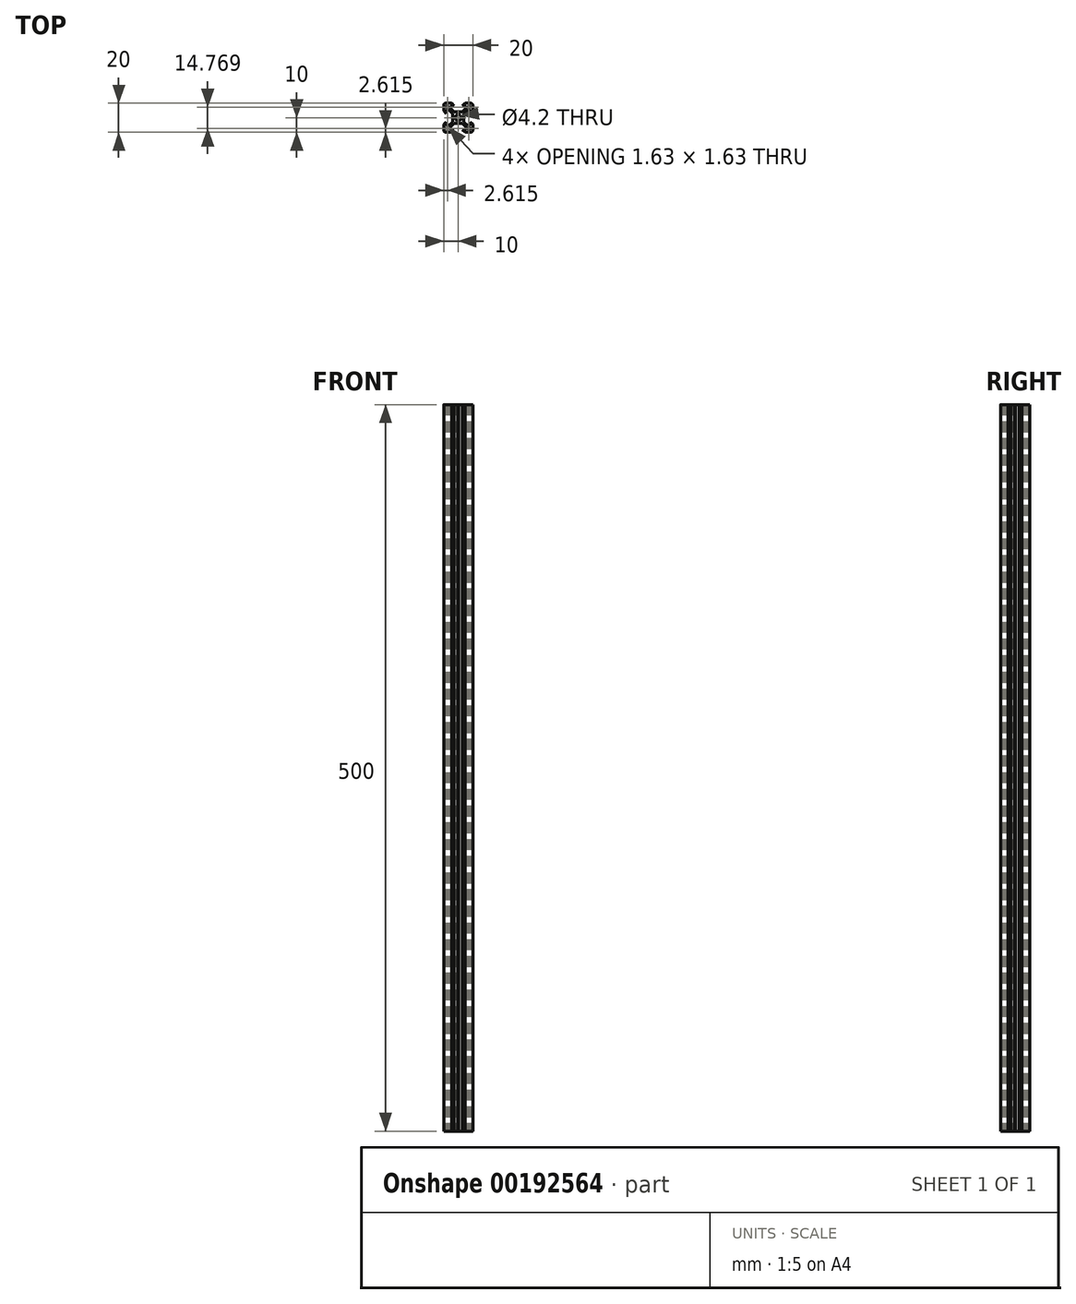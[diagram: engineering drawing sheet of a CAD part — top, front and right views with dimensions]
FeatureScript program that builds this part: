
annotation { "Feature Type Name" : "Feature", "Feature Type Description" : "" }
export const myFeature = defineFeature(function(context is Context, id is Id, definition is map)
    precondition{}
    {
        {
            var Q0;
            Q0=qCreatedBy(makeId("Top.planeOp"),FACE);
            var sketch = newSketch(context, id + "F0", { "sketchPlane" : qUnion([Q0])});
            skLineSegment(sketch, "E0", {"start": v(10, 8.5) * mm, "end": v(10, 4.64) * mm});
            skLineSegment(sketch, "E1", {"start": v(8.5, -10) * mm, "end": v(4.64, -10) * mm});
            skLineSegment(sketch, "E2", {"start": v(-10, -8.5) * mm, "end": v(-10, -4.64) * mm});
            skLineSegment(sketch, "E3", {"start": v(-8.5, 10) * mm, "end": v(-4.64, 10) * mm});
            skLineSegment(sketch, "E4.0", {"start": v(-5.5, 8.2) * mm, "end": v(-2.84, 8.2) * mm});
            skLineSegment(sketch, "E4.1", {"start": v(-8.2, -5.5) * mm, "end": v(-8.2, -2.84) * mm});
            skLineSegment(sketch, "E4.2", {"start": v(5.5, -8.2) * mm, "end": v(2.84, -8.2) * mm});
            skLineSegment(sketch, "E4.3", {"start": v(8.2, 5.5) * mm, "end": v(8.2, 2.84) * mm});
            skLineSegment(sketch, "E5.trimOffspring", {"start": v(4.64, 10) * mm, "end": v(8.5, 10) * mm});
            skPoint(sketch, "E6.start.orphan", {"position": v(0, 10) * mm});
            skLineSegment(sketch, "E7", {"start": v(-2.84, 8.2) * mm, "end": v(-4.64, 10) * mm});
            skLineSegment(sketch, "E8.trimOffspring", {"start": v(2.84, 8.2) * mm, "end": v(5.5, 8.2) * mm});
            skLineSegment(sketch, "E9.MirrorCS", {"start": v(2.84, 8.2) * mm, "end": v(4.64, 10) * mm});
            skLineSegment(sketch, "E10.MirrorCS", {"start": v(2.84, -8.2) * mm, "end": v(4.64, -10) * mm});
            skLineSegment(sketch, "E11.MirrorCS", {"start": v(-2.84, -8.2) * mm, "end": v(-4.64, -10) * mm});
            skLineSegment(sketch, "E12.trimOffspring", {"start": v(-2.84, -8.2) * mm, "end": v(-5.5, -8.2) * mm});
            skLineSegment(sketch, "E13.trimOffspring", {"start": v(-4.64, -10) * mm, "end": v(-8.5, -10) * mm});
            skLineSegment(sketch, "E14", {"start": v(-8.2, 2.84) * mm, "end": v(-10, 4.64) * mm});
            skLineSegment(sketch, "E15", {"start": v(-8.2, -2.84) * mm, "end": v(-10, -4.64) * mm});
            skLineSegment(sketch, "E16.trimOffspring", {"start": v(-10, 4.64) * mm, "end": v(-10, 8.5) * mm});
            skLineSegment(sketch, "E17.trimOffspring", {"start": v(-8.2, 2.84) * mm, "end": v(-8.2, 5.5) * mm});
            skLineSegment(sketch, "E18.MirrorCS", {"start": v(8.2, 2.84) * mm, "end": v(10, 4.64) * mm});
            skLineSegment(sketch, "E19.MirrorCS", {"start": v(8.2, -2.84) * mm, "end": v(10, -4.64) * mm});
            skLineSegment(sketch, "E20.trimOffspring", {"start": v(8.2, -2.84) * mm, "end": v(8.2, -5.5) * mm});
            skLineSegment(sketch, "E21.trimOffspring", {"start": v(10, -4.64) * mm, "end": v(10, -8.5) * mm});
            skCircle(sketch, "E22", {"center": v(0, 0) * mm, "radius": 2.1 * mm});
            skLineSegment(sketch, "E23", {"start": v(-6.56, 5.5) * mm, "end": v(-3.9, 2.84) * mm});
            skLineSegment(sketch, "E24", {"start": v(-5.5, 6.56) * mm, "end": v(-2.84, 3.9) * mm});
            skLineSegment(sketch, "E25", {"start": v(-5.5, 6.56) * mm, "end": v(-5.5, 8.2) * mm});
            skLineSegment(sketch, "E26", {"start": v(-6.56, 5.5) * mm, "end": v(-8.2, 5.5) * mm});
            skLineSegment(sketch, "E27", {"start": v(6.56, 5.5) * mm, "end": v(3.9, 2.84) * mm});
            skLineSegment(sketch, "E28", {"start": v(5.5, 6.56) * mm, "end": v(2.84, 3.9) * mm});
            skLineSegment(sketch, "E29", {"start": v(-6.56, -5.5) * mm, "end": v(-8.2, -5.5) * mm});
            skLineSegment(sketch, "E30", {"start": v(-5.5, -6.56) * mm, "end": v(-5.5, -8.2) * mm});
            skLineSegment(sketch, "E31", {"start": v(5.5, 6.56) * mm, "end": v(5.5, 8.2) * mm});
            skLineSegment(sketch, "E32", {"start": v(6.56, 5.5) * mm, "end": v(8.2, 5.5) * mm});
            skLineSegment(sketch, "E33", {"start": v(5.5, -6.56) * mm, "end": v(5.5, -8.2) * mm});
            skLineSegment(sketch, "E34", {"start": v(6.56, -5.5) * mm, "end": v(8.2, -5.5) * mm});
            skLineSegment(sketch, "E35.trimOffspring", {"start": v(2.84, -3.9) * mm, "end": v(5.5, -6.56) * mm});
            skLineSegment(sketch, "E36.trimOffspring", {"start": v(-2.84, -3.9) * mm, "end": v(-5.5, -6.56) * mm});
            skLineSegment(sketch, "E37.trimOffspring", {"start": v(-3.9, -2.84) * mm, "end": v(-6.56, -5.5) * mm});
            skLineSegment(sketch, "E38.trimOffspring", {"start": v(3.9, -2.84) * mm, "end": v(6.56, -5.5) * mm});
            skLineSegment(sketch, "E39", {"start": v(-3.9, -2.84) * mm, "end": v(-3.9, -0.25) * mm});
            skLineSegment(sketch, "E40", {"start": v(-2.84, 3.9) * mm, "end": v(-0.25, 3.9) * mm});
            skLineSegment(sketch, "E41", {"start": v(-2.84, -3.9) * mm, "end": v(-0.25, -3.9) * mm});
            skLineSegment(sketch, "E42", {"start": v(3.9, 2.84) * mm, "end": v(3.9, 0.25) * mm});
            skLineSegment(sketch, "E43", {"start": v(-8.2, 6.57) * mm, "end": v(-8.2, 8.2) * mm});
            skLineSegment(sketch, "E44", {"start": v(-6.57, 8.2) * mm, "end": v(-8.2, 8.2) * mm});
            skLineSegment(sketch, "E45", {"start": v(-8.2, 6.57) * mm, "end": v(-7.63, 6.57) * mm});
            skLineSegment(sketch, "E46", {"start": v(-6.57, 8.2) * mm, "end": v(-6.57, 7.63) * mm});
            skLineSegment(sketch, "E47", {"start": v(-7.63, 6.57) * mm, "end": v(-6.57, 7.63) * mm});
            skLineSegment(sketch, "E48.MirrorCS", {"start": v(6.57, 8.2) * mm, "end": v(8.2, 8.2) * mm});
            skLineSegment(sketch, "E49.MirrorCS", {"start": v(8.2, 6.57) * mm, "end": v(8.2, 8.2) * mm});
            skLineSegment(sketch, "E50.MirrorCS", {"start": v(8.2, 6.57) * mm, "end": v(7.63, 6.57) * mm});
            skLineSegment(sketch, "E51.MirrorCS", {"start": v(7.63, 6.57) * mm, "end": v(6.57, 7.63) * mm});
            skLineSegment(sketch, "E52.MirrorCS", {"start": v(6.57, 8.2) * mm, "end": v(6.57, 7.63) * mm});
            skLineSegment(sketch, "E53.MirrorCS", {"start": v(6.57, -8.2) * mm, "end": v(6.57, -7.63) * mm});
            skLineSegment(sketch, "E54.MirrorCS", {"start": v(8.2, -6.57) * mm, "end": v(7.63, -6.57) * mm});
            skLineSegment(sketch, "E55.MirrorCS", {"start": v(7.63, -6.57) * mm, "end": v(6.57, -7.63) * mm});
            skLineSegment(sketch, "E56.MirrorCS", {"start": v(6.57, -8.2) * mm, "end": v(8.2, -8.2) * mm});
            skLineSegment(sketch, "E57.MirrorCS", {"start": v(8.2, -6.57) * mm, "end": v(8.2, -8.2) * mm});
            skLineSegment(sketch, "E58.MirrorCS", {"start": v(-6.57, -8.2) * mm, "end": v(-8.2, -8.2) * mm});
            skLineSegment(sketch, "E59.MirrorCS", {"start": v(-8.2, -6.57) * mm, "end": v(-7.63, -6.57) * mm});
            skLineSegment(sketch, "E60.MirrorCS", {"start": v(-8.2, -6.57) * mm, "end": v(-8.2, -8.2) * mm});
            skLineSegment(sketch, "E61.MirrorCS", {"start": v(-7.63, -6.57) * mm, "end": v(-6.57, -7.63) * mm});
            skLineSegment(sketch, "E62.MirrorCS", {"start": v(-6.57, -8.2) * mm, "end": v(-6.57, -7.63) * mm});
            skPoint(sketch, "E63.visualSharp", {"position": v(-10, 10) * mm});
            skArc(sketch, "E63.filletArc", {"start": v(-8.5, 10) * mm, "mid": v(-9.56, 9.56) * mm, "end": v(-10, 8.5) * mm});
            skPoint(sketch, "E64.visualSharp", {"position": v(10, 10) * mm});
            skArc(sketch, "E64.filletArc", {"start": v(10, 8.5) * mm, "mid": v(9.56, 9.56) * mm, "end": v(8.5, 10) * mm});
            skPoint(sketch, "E65.visualSharp", {"position": v(10, -10) * mm});
            skArc(sketch, "E65.filletArc", {"start": v(8.5, -10) * mm, "mid": v(9.56, -9.56) * mm, "end": v(10, -8.5) * mm});
            skPoint(sketch, "E66.visualSharp", {"position": v(-10, -10) * mm});
            skArc(sketch, "E66.filletArc", {"start": v(-10, -8.5) * mm, "mid": v(-9.56, -9.56) * mm, "end": v(-8.5, -10) * mm});
            skLineSegment(sketch, "E67", {"start": v(-3.65, 0) * mm, "end": v(-3.9, 0.25) * mm});
            skLineSegment(sketch, "E68.MirrorCS", {"start": v(-3.65, 0) * mm, "end": v(-3.9, -0.25) * mm});
            skLineSegment(sketch, "E69.trimOffspring", {"start": v(-3.9, 0.25) * mm, "end": v(-3.9, 2.84) * mm});
            skLineSegment(sketch, "E70.MirrorCS", {"start": v(3.65, 0) * mm, "end": v(3.9, 0.25) * mm});
            skLineSegment(sketch, "E71.MirrorCS", {"start": v(3.65, 0) * mm, "end": v(3.9, -0.25) * mm});
            skLineSegment(sketch, "E72", {"start": v(0, -3.65) * mm, "end": v(0.25, -3.9) * mm});
            skLineSegment(sketch, "E73.MirrorCS", {"start": v(0, -3.65) * mm, "end": v(-0.25, -3.9) * mm});
            skLineSegment(sketch, "E74.trimOffspring", {"start": v(0.25, -3.9) * mm, "end": v(2.84, -3.9) * mm});
            skLineSegment(sketch, "E75.trimOffspring", {"start": v(3.9, -0.25) * mm, "end": v(3.9, -2.84) * mm});
            skLineSegment(sketch, "E76.MirrorCS", {"start": v(0, 3.65) * mm, "end": v(-0.25, 3.9) * mm});
            skLineSegment(sketch, "E77.MirrorCS", {"start": v(0, 3.65) * mm, "end": v(0.25, 3.9) * mm});
            skLineSegment(sketch, "E78.trimOffspring", {"start": v(0.25, 3.9) * mm, "end": v(2.84, 3.9) * mm});
            skSolve(sketch);
        }
        {
            var Q0;
            Q0=makeQuery(id+"F0.imprint","IMPRINT",FACE,{"disambiguationData":[TD([[makeQuery(id+"F0.imprint","IMPRINT",EDGE,{"derivedFrom":sQuery(id+"F0.wireOp",EDGE,"E0")}),-1.0]])]});
            extrude(context, id + "F1", {"entities" : qUnion([Q0]), "depth" : 500 * mm});
        }
    });
